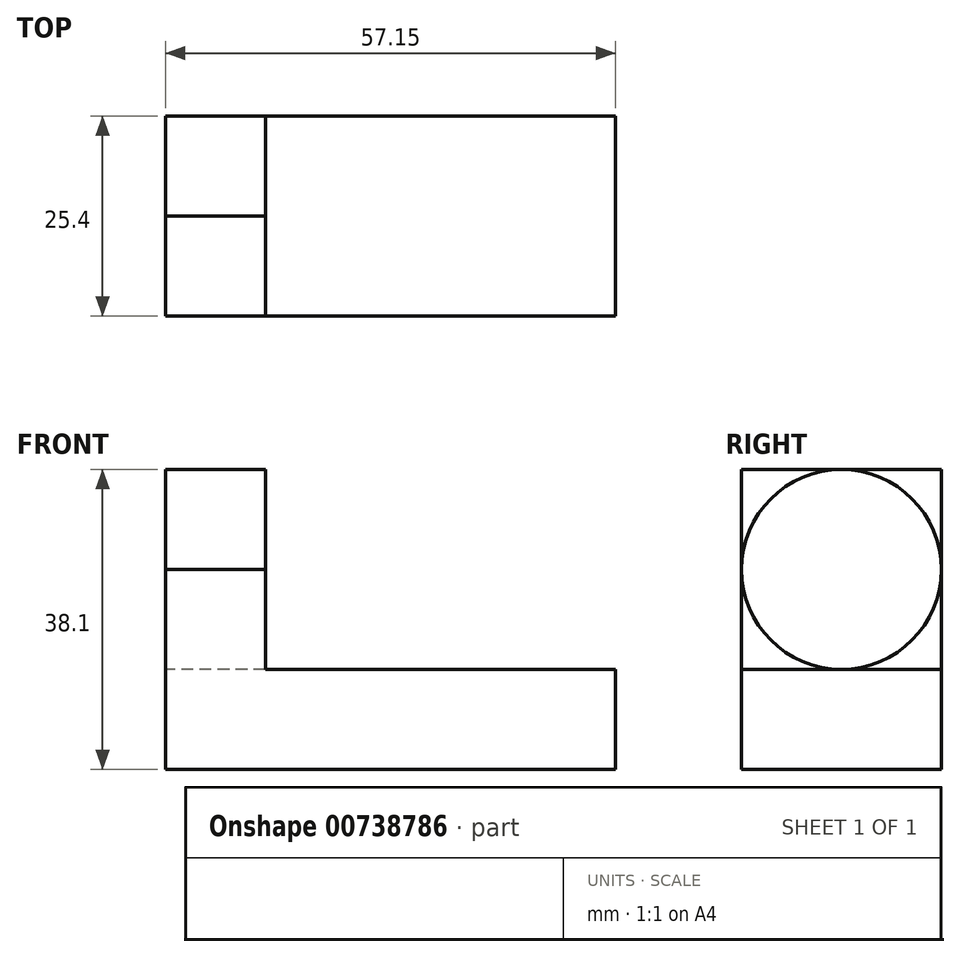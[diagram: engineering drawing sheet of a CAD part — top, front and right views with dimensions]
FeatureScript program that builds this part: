
annotation { "Feature Type Name" : "Feature", "Feature Type Description" : "" }
export const myFeature = defineFeature(function(context is Context, id is Id, definition is map)
    precondition{}
    {
        {
            var Q0;
            Q0=qCreatedBy(makeId("Front.planeOp"),FACE);
            var sketch = newSketch(context, id + "F0", { "sketchPlane" : qUnion([Q0])});
            skLineSegment(sketch, "E0", {"start": v(0, 0) * mm, "end": v(0, 38.1) * mm});
            skLineSegment(sketch, "E1", {"start": v(0, 38.1) * mm, "end": v(12.7, 38.1) * mm});
            skLineSegment(sketch, "E2", {"start": v(12.7, 38.1) * mm, "end": v(12.7, 12.7) * mm});
            skLineSegment(sketch, "E3", {"start": v(12.7, 12.7) * mm, "end": v(57.15, 12.7) * mm});
            skLineSegment(sketch, "E4", {"start": v(57.15, 12.7) * mm, "end": v(57.15, 0) * mm});
            skLineSegment(sketch, "E5", {"start": v(57.15, 0) * mm, "end": v(0, 0) * mm});
            skSolve(sketch);
        }
        {
            var Q0;
            Q0 = qSketchRegion(id + "F0", true);
            extrude(context, id + "F1", {"entities" : qUnion([Q0]), "depth" : 25.4 * mm, "offsetDistance" : 25.4 * mm});
        }
        {
            var Q0;
            Q0=qCreatedBy(makeId("Right.planeOp"),FACE);
            var sketch = newSketch(context, id + "F2", { "sketchPlane" : qUnion([Q0])});
            skLineSegment(sketch, "E6", {"start": v(-12.7, 38.1) * mm, "end": v(-12.7, 12.7) * mm});
            skLineSegment(sketch, "E7", {"start": v(-25.4, 25.4) * mm, "end": v(0, 25.4) * mm});
            skCircle(sketch, "E8", {"center": v(-12.7, 25.4) * mm, "radius": 12.7 * mm});
            skArc(sketch, "E9", {"start": v(-19.05, 38.1) * mm, "mid": v(-12.7, 25.4) * mm, "end": v(-6.35, 38.1) * mm});
            skSolve(sketch);
        }
        {
            var Q0;
            {var subQ0=sQuery(id+"F2.wireOp",EDGE,"E8");var subQ1=sQuery(id+"F2.wireOp",EDGE,"E6");var subQ2=makeQuery(id+"F2.imprint","INTERSECT",VERTEX,{"disambiguationData":[OD(0.0)],"derivedFrom":[subQ1,subQ0]});Q0=makeQuery(id+"F2.imprint","IMPRINT",FACE,{"disambiguationData":[TD([[makeQuery(id+"F2.imprint","IMPRINT",EDGE,{"disambiguationData":[TD([[subQ2,1.0]])],"derivedFrom":subQ0}),1.0]])]});}
            var Q1;
            {var subQ0=sQuery(id+"F2.wireOp",EDGE,"E8");var subQ1=sQuery(id+"F2.wireOp",EDGE,"E6");var subQ2=makeQuery(id+"F2.imprint","INTERSECT",VERTEX,{"disambiguationData":[OD(0.0)],"derivedFrom":[subQ1,subQ0]});Q1=makeQuery(id+"F2.imprint","IMPRINT",FACE,{"disambiguationData":[TD([[makeQuery(id+"F2.imprint","IMPRINT",EDGE,{"disambiguationData":[TD([[subQ2,-1.0]])],"derivedFrom":subQ0}),1.0]])]});}
            extrude(context, id + "F3", {"entities" : qUnion([Q0, Q1]), "operationType" : NewBodyOperationType.REMOVE, "endBound" : BoundingType.THROUGH_ALL, "depth" : 25.4 * mm, "offsetDistance" : 25.4 * mm});
        }
        {
            var Q0;
            Q0 = qSketchRegion(id + "F2", true);
            extrude(context, id + "F4", {"entities" : qUnion([Q0]), "operationType" : NewBodyOperationType.REMOVE, "depth" : 25.4 * mm, "offsetDistance" : 25.4 * mm});
        }
    });
